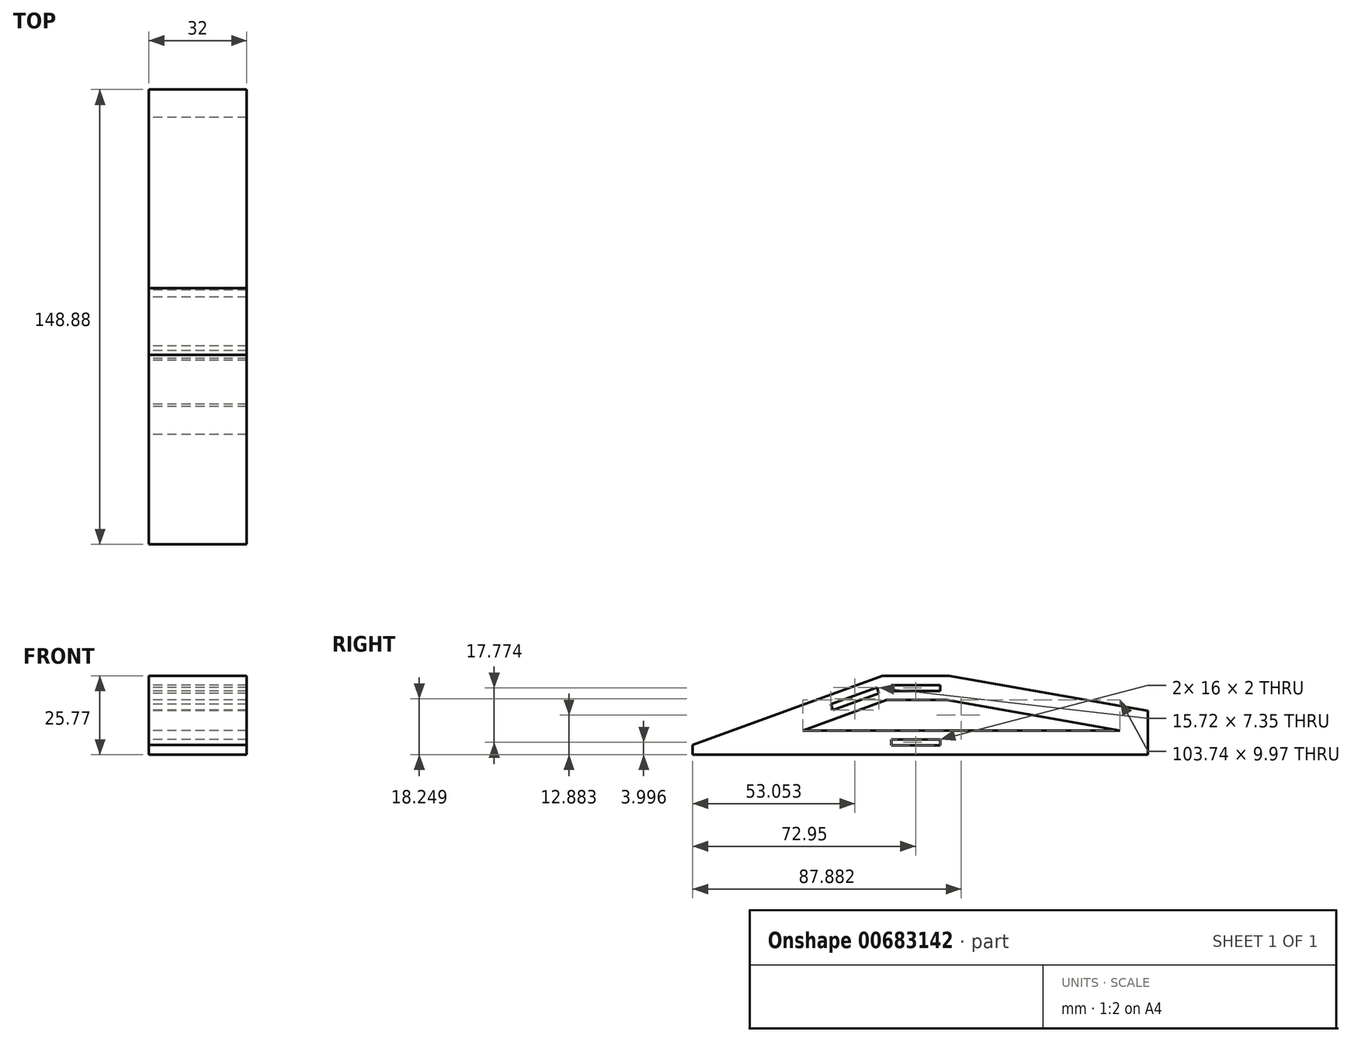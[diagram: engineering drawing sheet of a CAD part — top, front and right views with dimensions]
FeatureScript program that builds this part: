
annotation { "Feature Type Name" : "Feature", "Feature Type Description" : "" }
export const myFeature = defineFeature(function(context is Context, id is Id, definition is map)
    precondition{}
    {
        {
            var Q0;
            Q0=qCreatedBy(makeId("Right.planeOp"),FACE);
            var sketch = newSketch(context, id + "F0", { "sketchPlane" : qUnion([Q0])});
            skLineSegment(sketch, "E0", {"start": v(-10.93, 0) * mm, "end": v(10.93, 0) * mm});
            skLineSegment(sketch, "E1", {"start": v(-10.93, 0) * mm, "end": v(-72.95, -22.57) * mm});
            skLineSegment(sketch, "E2", {"start": v(-72.95, -22.57) * mm, "end": v(-72.95, -25.77) * mm});
            skLineSegment(sketch, "E3", {"start": v(-72.95, -25.77) * mm, "end": v(75.93, -25.77) * mm});
            skLineSegment(sketch, "E4", {"start": v(75.93, -25.77) * mm, "end": v(75.93, -11.46) * mm});
            skLineSegment(sketch, "E5", {"start": v(75.93, -11.46) * mm, "end": v(10.93, 0) * mm});
            skLineSegment(sketch, "E6", {"start": v(0, 0) * mm, "end": v(0, -3) * mm, "construction": true});
            skLineSegment(sketch, "E7", {"start": v(0, -3) * mm, "end": v(0, -4) * mm, "construction": true});
            skLineSegment(sketch, "E8.bottom", {"start": v(8, -5) * mm, "end": v(-8, -5) * mm});
            skLineSegment(sketch, "E8.top", {"start": v(8, -3) * mm, "end": v(-8, -3) * mm});
            skLineSegment(sketch, "E8.left", {"start": v(8, -5) * mm, "end": v(8, -3) * mm});
            skLineSegment(sketch, "E8.right", {"start": v(-8, -5) * mm, "end": v(-8, -3) * mm});
            skPoint(sketch, "E8.middle", {"position": v(0, -4) * mm});
            skLineSegment(sketch, "E9", {"start": v(0, -25.77) * mm, "end": v(0, -21.77) * mm, "construction": true});
            skLineSegment(sketch, "E10.bottom", {"start": v(8, -20.77) * mm, "end": v(-8, -20.77) * mm});
            skLineSegment(sketch, "E10.top", {"start": v(8, -22.77) * mm, "end": v(-8, -22.77) * mm});
            skLineSegment(sketch, "E10.left", {"start": v(8, -20.77) * mm, "end": v(8, -22.77) * mm});
            skLineSegment(sketch, "E10.right", {"start": v(-8, -20.77) * mm, "end": v(-8, -22.77) * mm});
            skPoint(sketch, "E10.middle", {"position": v(0, -21.77) * mm});
            skLineSegment(sketch, "E11", {"start": v(-10.93, 0) * mm, "end": v(-9.56, -3.76) * mm, "construction": true});
            skLineSegment(sketch, "E12", {"start": v(-9.56, -3.76) * mm, "end": v(-12.38, -4.78) * mm, "construction": true});
            skLineSegment(sketch, "E13", {"start": v(-12.72, -3.85) * mm, "end": v(-27.76, -9.32) * mm});
            skLineSegment(sketch, "E14", {"start": v(-27.76, -9.32) * mm, "end": v(-27.07, -11.2) * mm});
            skLineSegment(sketch, "E15", {"start": v(-12.38, -4.78) * mm, "end": v(-12.04, -5.72) * mm});
            skLineSegment(sketch, "E16", {"start": v(-12.04, -5.72) * mm, "end": v(-27.07, -11.2) * mm});
            skLineSegment(sketch, "E17", {"start": v(-12.72, -3.85) * mm, "end": v(-12.38, -4.78) * mm});
            skLineSegment(sketch, "E18.0", {"start": v(-9.53, -7.9) * mm, "end": v(-36.94, -17.87) * mm});
            skLineSegment(sketch, "E18.1", {"start": v(-9.53, -7.9) * mm, "end": v(10.24, -7.9) * mm});
            skLineSegment(sketch, "E18.2", {"start": v(66.8, -17.87) * mm, "end": v(10.24, -7.9) * mm});
            skLineSegment(sketch, "E18.3", {"start": v(-36.94, -17.87) * mm, "end": v(66.8, -17.87) * mm});
            skSolve(sketch);
        }
        {
            var Q0;
            Q0=makeQuery(id+"F0.imprint","IMPRINT",FACE,{"disambiguationData":[TD([[makeQuery(id+"F0.imprint","IMPRINT",EDGE,{"derivedFrom":sQuery(id+"F0.wireOp",EDGE,"E0")}),-1.0]])]});
            extrude(context, id + "F1", {"entities" : qUnion([Q0]), "endBound" : BoundingType.SYMMETRIC, "depth" : 32 * mm, "offsetDistance" : 25 * mm});
        }
    });
